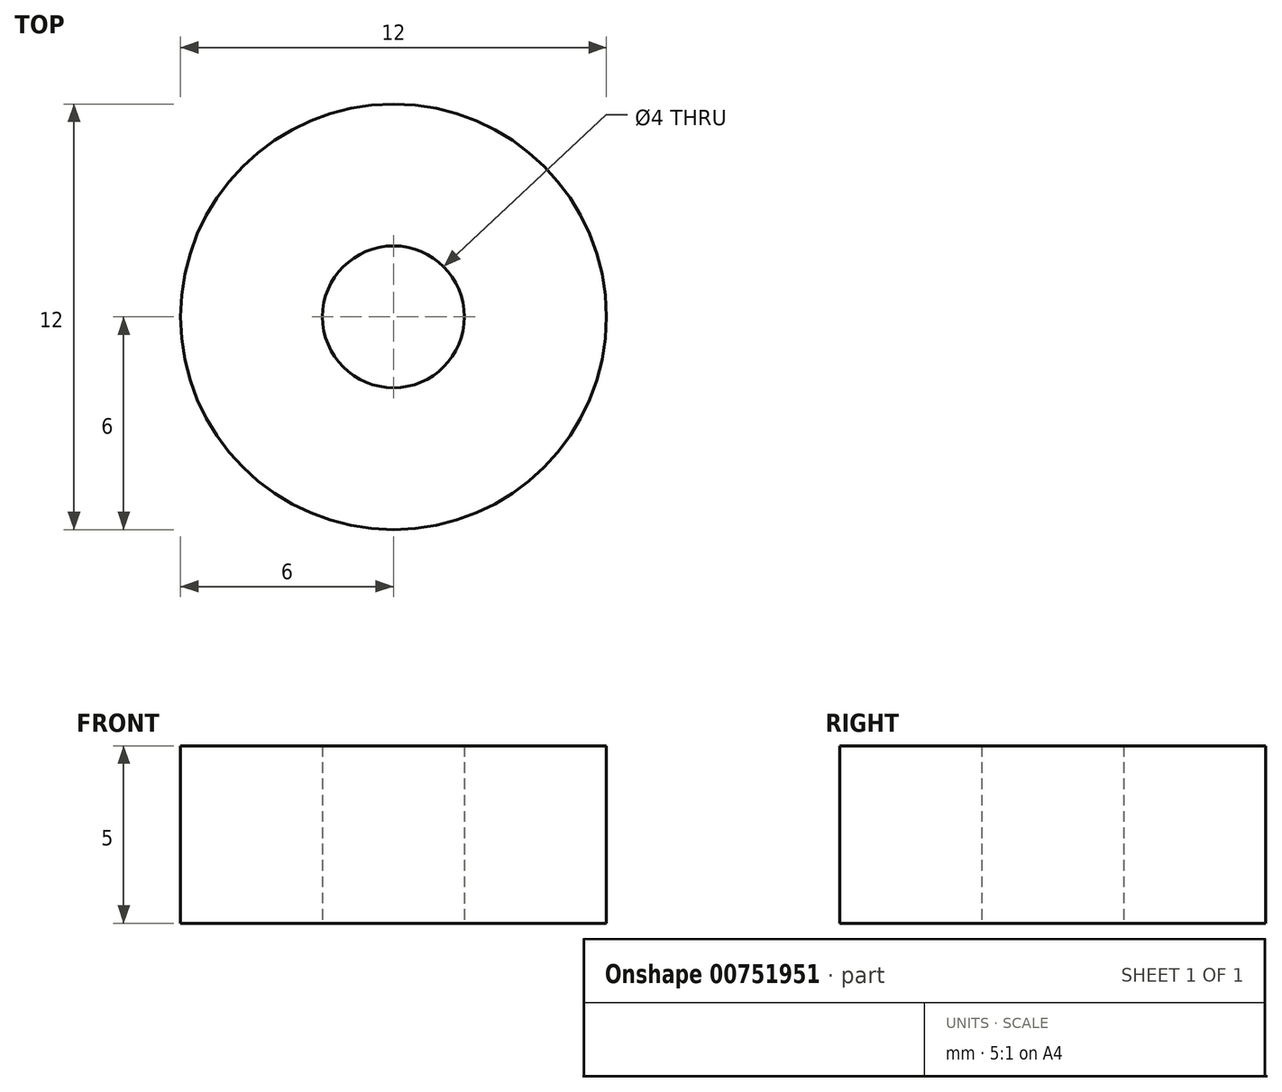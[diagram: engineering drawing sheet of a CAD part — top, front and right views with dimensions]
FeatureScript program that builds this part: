
annotation { "Feature Type Name" : "Feature", "Feature Type Description" : "" }
export const myFeature = defineFeature(function(context is Context, id is Id, definition is map)
    precondition{}
    {
        {
            var Q0;
            Q0=qCreatedBy(makeId("Top.planeOp"),FACE);
            var sketch = newSketch(context, id + "F0", { "sketchPlane" : qUnion([Q0])});
            skCircle(sketch, "E0", {"center": v(0, 0) * mm, "radius": 6 * mm});
            skCircle(sketch, "E1", {"center": v(0, 0) * mm, "radius": 2 * mm});
            skSolve(sketch);
        }
        {
            var Q0;
            Q0 = qSketchRegion(id + "F0", true);
            extrude(context, id + "F1", {"entities" : qUnion([Q0]), "depth" : 5 * mm, "offsetDistance" : 25 * mm});
        }
    });
